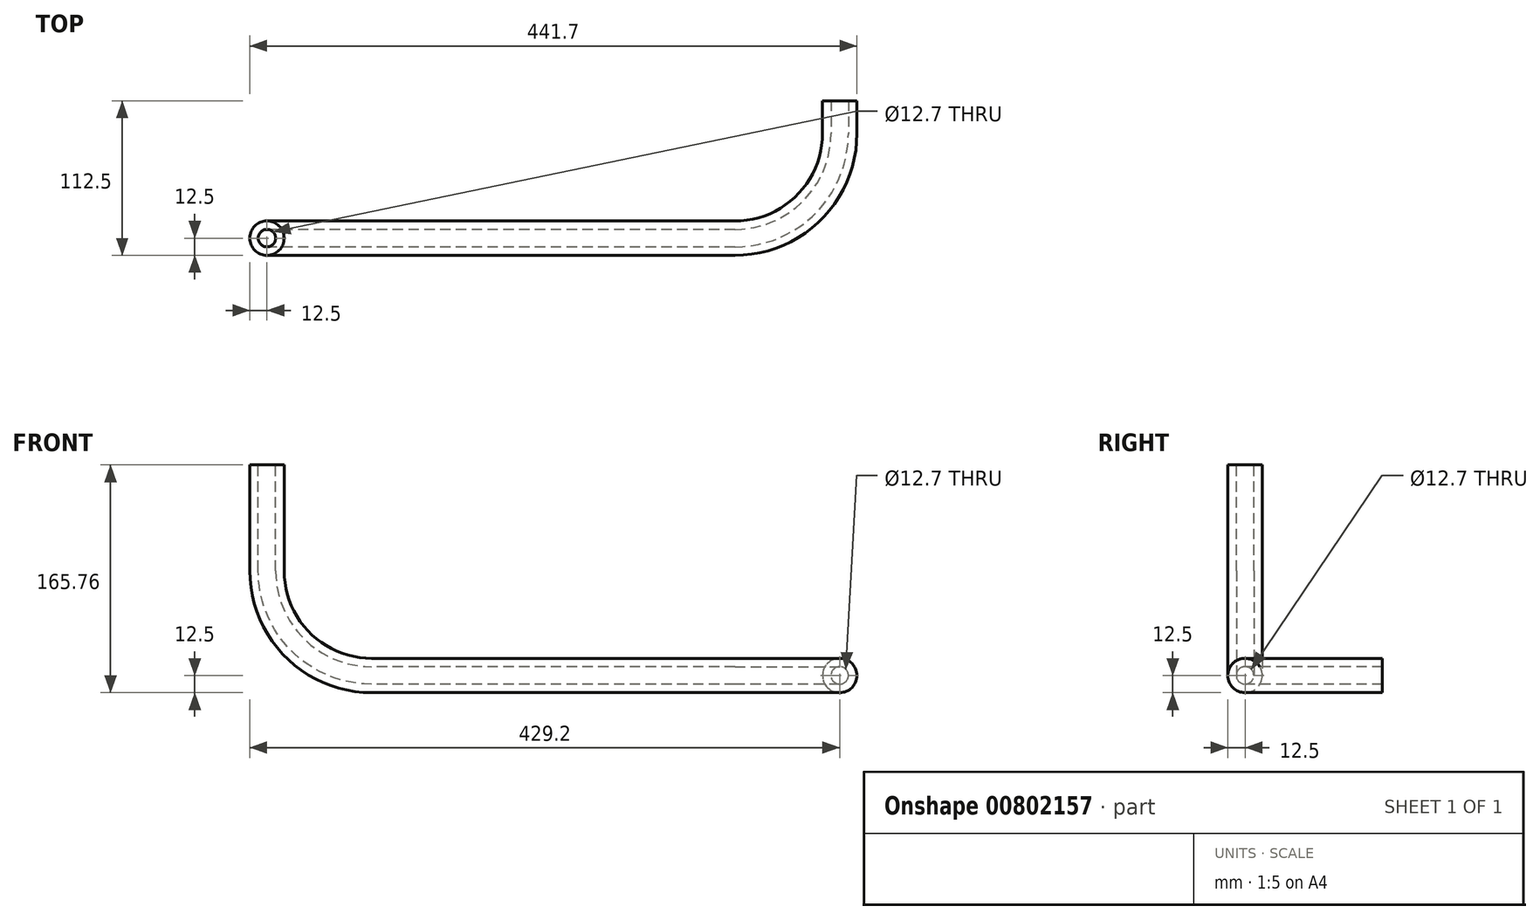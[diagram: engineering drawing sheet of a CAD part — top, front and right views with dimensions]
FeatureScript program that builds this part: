
annotation { "Feature Type Name" : "Feature", "Feature Type Description" : "" }
export const myFeature = defineFeature(function(context is Context, id is Id, definition is map)
    precondition{}
    {
        {
            var Q0;
            Q0=qCreatedBy(makeId("Front.planeOp"),FACE);
            var sketch = newSketch(context, id + "F0", { "sketchPlane" : qUnion([Q0])});
            skCircle(sketch, "E0", {"center": v(0, 0) * mm, "radius": 6.35 * mm});
            skCircle(sketch, "E1", {"center": v(0, 0) * mm, "radius": 12.5 * mm});
            skSolve(sketch);
        }
        {
            var Q0;
            Q0=qCreatedBy(makeId("Top.planeOp"),FACE);
            var sketch = newSketch(context, id + "F1", { "sketchPlane" : qUnion([Q0])});
            skLineSegment(sketch, "E2", {"start": v(0, 0) * mm, "end": v(0, -23.8) * mm});
            skLineSegment(sketch, "E3", {"start": v(-76.2, -100) * mm, "end": v(-340.5, -100) * mm});
            skPoint(sketch, "E4.visualSharp", {"position": v(0, -100) * mm});
            skArc(sketch, "E4.filletArc", {"start": v(-76.2, -100) * mm, "mid": v(-22.32, -77.68) * mm, "end": v(0, -23.8) * mm});
            skSolve(sketch);
        }
        {
            var Q0;
            Q0=qCreatedBy(makeId("Front.planeOp"),FACE);
            cPlane(context, id + "F2", {"entities" : qUnion([Q0]), "cplaneType" : CPlaneType.OFFSET, "offset" : 100 * mm, "width" : 150 * mm, "height" : 150 * mm});
        }
        {
            var Q0;
            Q0=qCreatedBy(id+"F2.planeOp",FACE);
            var sketch = newSketch(context, id + "F3", { "sketchPlane" : qUnion([Q0])});
            skLineSegment(sketch, "E5", {"start": v(-340.5, 0) * mm, "end": v(-340.5, 76.2) * mm, "construction": true});
            skArc(sketch, "E6", {"start": v(-340.5, 0) * mm, "mid": v(-394.38, 22.32) * mm, "end": v(-416.7, 76.2) * mm});
            skLineSegment(sketch, "E7", {"start": v(-416.7, 76.2) * mm, "end": v(-416.7, 153.26) * mm});
            skSolve(sketch);
        }
        {
            var Q0;
            Q0=qSketchRegion(id+"F0",true);
            var Q1;
            Q1=qConstructionFilter(qBodyType(qCreatedBy(id+"F1",EDGE),BodyType.WIRE),ConstructionObject.NO);
            var Q2;
            Q2=qConstructionFilter(qBodyType(qCreatedBy(id+"F3",EDGE),BodyType.WIRE),ConstructionObject.NO);
            sweep(context, id + "F4", {"profiles" : qUnion([Q0]), "path" : qUnion([Q1, Q2])});
        }
    });
